# Revit family: P190780JX-160c_JXW8530HS_StainlessSteel_JA_Cooking_Ventilation
name_source: partatom
category: Specialty Equipment
units: mm (PartAtom-declared; Revit-internal decimal feet)

## family parameters
Always vertical = Yes
Cut with Voids When Loaded = No
Enable Cutting in Views = No
Maintain Annotation Orientation = No
Part Type = Normal
Room Calculation Point = No
Round Connector Dimension = Use Diameter
Shared = No
Work Plane-Based = No

## types (1)
- JXW8530HS
    Accent Material = ARCAT - Metal - Steel - Gray
    Amps = 15 A
    Body Material = ARCAT - Metal - Steel - Stainless
    Default Elevation = 0"
    Depth = 19 11/16"
    Description = Pyramid Style Canopy Wall Hood, 30”
Hotte murale de style pyramidal en acier lustré, 30 po
    Family Name = WALL HOODS - 30"
    Feature 1 = Glass-Touch Controls
Commandes à effleurement sous verre
    Feature 2 = Lustre Stainless
Acier inoxydable lustré
    Feature 3 = Wall Mount Hood
Hotte murale
    Height = 5"
    Installation-Fabrication = http://access.whirlpool.com Instruction&sku=JXW8530HS&language=EN
http://access.whirlpool.com Instruction&sku=JXW8530HS&language=EN
    Manufacturer = Jenn Air
    Model = JXW8530HS
    Voltage = 0 V
    Width = 30"

## geometry (parser evidence)
native form markers: Sweep x4
no freeform markers — native parametric forms only
